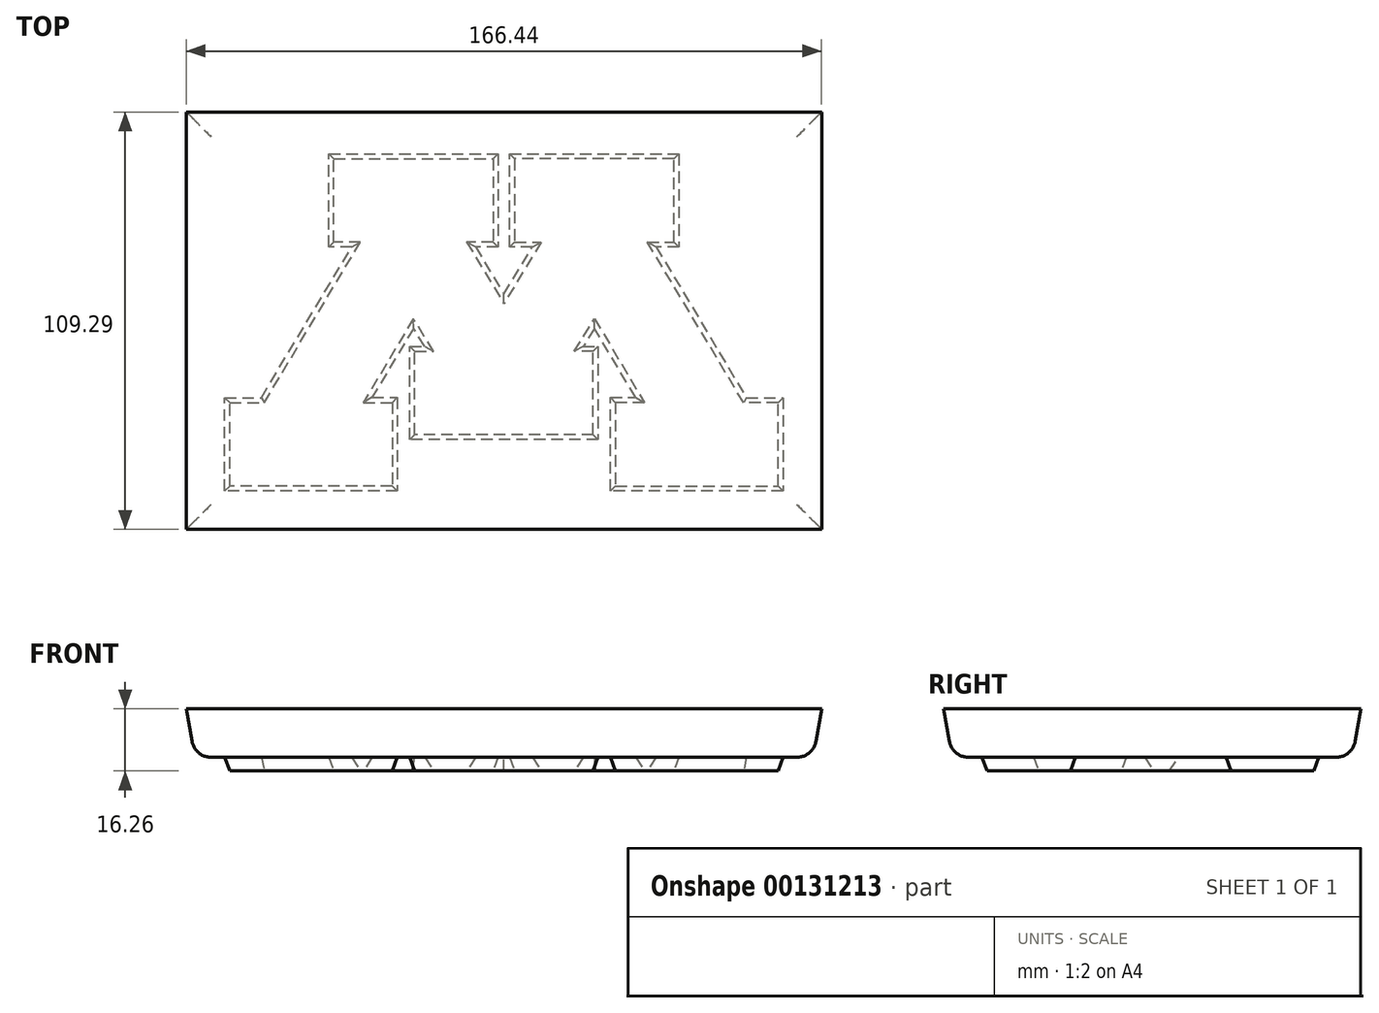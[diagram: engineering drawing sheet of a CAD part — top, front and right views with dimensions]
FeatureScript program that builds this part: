
annotation { "Feature Type Name" : "Feature", "Feature Type Description" : "" }
export const myFeature = defineFeature(function(context is Context, id is Id, definition is map)
    precondition{}
    {
        {
            var Q0;
            Q0=qCreatedBy(makeId("Top.planeOp"),FACE);
            var sketch = newSketch(context, id + "F0", { "sketchPlane" : qUnion([Q0])});
            skLineSegment(sketch, "E0", {"start": v(0, 13.9) * mm, "end": v(-9.74, 30.03) * mm});
            skLineSegment(sketch, "E1", {"start": v(-9.74, 30.03) * mm, "end": v(-2.82, 30.03) * mm});
            skLineSegment(sketch, "E2", {"start": v(-2.82, 30.03) * mm, "end": v(-2.82, 51.81) * mm});
            skLineSegment(sketch, "E3", {"start": v(-2.82, 51.81) * mm, "end": v(-44.55, 51.81) * mm});
            skLineSegment(sketch, "E4", {"start": v(-44.55, 51.81) * mm, "end": v(-44.55, 30.06) * mm});
            skLineSegment(sketch, "E5", {"start": v(-44.55, 30.06) * mm, "end": v(-37.59, 30.06) * mm});
            skLineSegment(sketch, "E6", {"start": v(-37.59, 30.06) * mm, "end": v(-62.78, -12) * mm});
            skLineSegment(sketch, "E7", {"start": v(-62.78, -12) * mm, "end": v(-71.82, -12) * mm});
            skLineSegment(sketch, "E8", {"start": v(-71.82, -12) * mm, "end": v(-71.82, -33.84) * mm});
            skLineSegment(sketch, "E9", {"start": v(-71.82, -33.84) * mm, "end": v(-29.23, -33.84) * mm});
            skLineSegment(sketch, "E10", {"start": v(-29.23, -33.84) * mm, "end": v(-29.23, -11.96) * mm});
            skLineSegment(sketch, "E11", {"start": v(-29.23, -11.96) * mm, "end": v(-36.81, -11.96) * mm});
            skLineSegment(sketch, "E12", {"start": v(-36.81, -11.96) * mm, "end": v(-23.72, 9.93) * mm});
            skLineSegment(sketch, "E13", {"start": v(-23.72, 9.93) * mm, "end": v(-18.44, 1.4) * mm});
            skLineSegment(sketch, "E14", {"start": v(-18.44, 1.4) * mm, "end": v(-23.37, 1.4) * mm});
            skLineSegment(sketch, "E15", {"start": v(-23.37, 1.4) * mm, "end": v(-23.37, -20.36) * mm});
            skLineSegment(sketch, "E16", {"start": v(-23.37, -20.36) * mm, "end": v(0, -20.36) * mm});
            skLineSegment(sketch, "E17", {"start": v(0, -20.36) * mm, "end": v(0, 13.9) * mm});
            skSolve(sketch);
        }
        {
            var Q0;
            Q0=qSketchRegion(id+"F0",true);
            extrude(context, id + "F1", {"entities" : qUnion([Q0]), "depth" : 12.45 * mm, "hasDraft" : true, "draftAngle" : 20 * degree});
        }
        {
            var Q0;
            Q0=makeQuery(id+"F1.opExtrude","SWEPT_BODY",BODY,{"disambiguationData":[OSD([sQuery(id+"F0.wireOp",EDGE,"E0"),sQuery(id+"F0.wireOp",EDGE,"E1"),sQuery(id+"F0.wireOp",EDGE,"E2"),sQuery(id+"F0.wireOp",EDGE,"E3"),sQuery(id+"F0.wireOp",EDGE,"E4"),sQuery(id+"F0.wireOp",EDGE,"E5"),sQuery(id+"F0.wireOp",EDGE,"E6"),sQuery(id+"F0.wireOp",EDGE,"E7"),sQuery(id+"F0.wireOp",EDGE,"E8"),sQuery(id+"F0.wireOp",EDGE,"E9"),sQuery(id+"F0.wireOp",EDGE,"E10"),sQuery(id+"F0.wireOp",EDGE,"E11"),sQuery(id+"F0.wireOp",EDGE,"E12"),sQuery(id+"F0.wireOp",EDGE,"E13"),sQuery(id+"F0.wireOp",EDGE,"E14"),sQuery(id+"F0.wireOp",EDGE,"E15"),sQuery(id+"F0.wireOp",EDGE,"E16"),sQuery(id+"F0.wireOp",EDGE,"E17")])]});
            var Q1;
            Q1=qCreatedBy(makeId("Right.planeOp"),FACE);
            mirror(context, id + "F2", {"operationType" : NewBodyOperationType.ADD, "entities" : qUnion([Q0]), "mirrorPlane" : qUnion([Q1])});
        }
        {
            var Q0;
            {var subQ0=makeQuery(id+"F1.opExtrude","CAP_FACE",FACE,{"disambiguationData":[OSD([sQuery(id+"F0.wireOp",EDGE,"E0"),sQuery(id+"F0.wireOp",EDGE,"E1"),sQuery(id+"F0.wireOp",EDGE,"E2"),sQuery(id+"F0.wireOp",EDGE,"E3"),sQuery(id+"F0.wireOp",EDGE,"E4"),sQuery(id+"F0.wireOp",EDGE,"E5"),sQuery(id+"F0.wireOp",EDGE,"E6"),sQuery(id+"F0.wireOp",EDGE,"E7"),sQuery(id+"F0.wireOp",EDGE,"E8"),sQuery(id+"F0.wireOp",EDGE,"E9"),sQuery(id+"F0.wireOp",EDGE,"E10"),sQuery(id+"F0.wireOp",EDGE,"E11"),sQuery(id+"F0.wireOp",EDGE,"E12"),sQuery(id+"F0.wireOp",EDGE,"E13"),sQuery(id+"F0.wireOp",EDGE,"E14"),sQuery(id+"F0.wireOp",EDGE,"E15"),sQuery(id+"F0.wireOp",EDGE,"E16"),sQuery(id+"F0.wireOp",EDGE,"E17")])],"isStart":false});Q0=makeQuery(id+"F2.boolean.opBoolean","MERGE",FACE,{"derivedFrom":[subQ0,makeQuery(id+"F2.opPattern","COPY",FACE,{"derivedFrom":subQ0,"instanceName":"1"})]});}
            var sketch = newSketch(context, id + "F3", { "sketchPlane" : qUnion([Q0])});
            skLineSegment(sketch, "E18.bottom", {"start": v(-82.55, -44.51) * mm, "end": v(82.55, -44.51) * mm});
            skLineSegment(sketch, "E18.top", {"start": v(-82.55, 63.44) * mm, "end": v(82.55, 63.44) * mm});
            skLineSegment(sketch, "E18.left", {"start": v(-82.55, -44.51) * mm, "end": v(-82.55, 63.44) * mm});
            skLineSegment(sketch, "E18.right", {"start": v(82.55, -44.51) * mm, "end": v(82.55, 63.44) * mm});
            skPoint(sketch, "E18.middle", {"position": v(0, 9.46) * mm});
            skSolve(sketch);
        }
        {
            var Q0;
            Q0 = qSketchRegion(id + "F3", true);
            extrude(context, id + "F4", {"entities" : qUnion([Q0]), "operationType" : NewBodyOperationType.ADD, "oppositeDirection" : true, "depth" : 8.9 * mm, "hasDraft" : true, "draftAngle" : 10 * degree, "draftPullDirection" : true});
        }
        {
            var Q0;
            {var subQ0=makeQuery(id+"F1.opExtrude","CAP_FACE",FACE,{"disambiguationData":[OSD([sQuery(id+"F0.wireOp",EDGE,"E0"),sQuery(id+"F0.wireOp",EDGE,"E1"),sQuery(id+"F0.wireOp",EDGE,"E2"),sQuery(id+"F0.wireOp",EDGE,"E3"),sQuery(id+"F0.wireOp",EDGE,"E4"),sQuery(id+"F0.wireOp",EDGE,"E5"),sQuery(id+"F0.wireOp",EDGE,"E6"),sQuery(id+"F0.wireOp",EDGE,"E7"),sQuery(id+"F0.wireOp",EDGE,"E8"),sQuery(id+"F0.wireOp",EDGE,"E9"),sQuery(id+"F0.wireOp",EDGE,"E10"),sQuery(id+"F0.wireOp",EDGE,"E11"),sQuery(id+"F0.wireOp",EDGE,"E12"),sQuery(id+"F0.wireOp",EDGE,"E13"),sQuery(id+"F0.wireOp",EDGE,"E14"),sQuery(id+"F0.wireOp",EDGE,"E15"),sQuery(id+"F0.wireOp",EDGE,"E16"),sQuery(id+"F0.wireOp",EDGE,"E17")])],"isStart":false});Q0=makeQuery(id+"F4.boolean.opBoolean","MERGE",FACE,{"derivedFrom":[makeQuery(id+"F2.boolean.opBoolean","MERGE",FACE,{"derivedFrom":[subQ0,makeQuery(id+"F2.opPattern","COPY",FACE,{"derivedFrom":subQ0,"instanceName":"1"})]}),makeQuery(id+"F4.opExtrude","CAP_FACE",FACE,{"disambiguationData":[OSD([sQuery(id+"F3.wireOp",EDGE,"E18.bottom"),sQuery(id+"F3.wireOp",EDGE,"E18.top"),sQuery(id+"F3.wireOp",EDGE,"E18.left"),sQuery(id+"F3.wireOp",EDGE,"E18.right")])],"isStart":true})]});}
            extrude(context, id + "F5", {"entities" : qUnion([Q0]), "operationType" : NewBodyOperationType.ADD, "depth" : 3.8 * mm, "hasDraft" : true, "draftAngle" : 10 * degree});
        }
        {
            var Q0;
            Q0=makeQuery(id+"F4.opExtrude","CAP_EDGE",EDGE,{"disambiguationData":[OSD([sQuery(id+"F3.wireOp",EDGE,"E18.right")])],"isStart":false});
            var Q1;
            Q1=makeQuery(id+"F4.opExtrude","CAP_EDGE",EDGE,{"disambiguationData":[OSD([sQuery(id+"F3.wireOp",EDGE,"E18.top")])],"isStart":false});
            var Q2;
            Q2=makeQuery(id+"F4.opExtrude","CAP_EDGE",EDGE,{"disambiguationData":[OSD([sQuery(id+"F3.wireOp",EDGE,"E18.bottom")])],"isStart":false});
            var Q3;
            Q3=makeQuery(id+"F4.opExtrude","CAP_EDGE",EDGE,{"disambiguationData":[OSD([sQuery(id+"F3.wireOp",EDGE,"E18.left")])],"isStart":false});
            fillet(context, id + "F6", {"entities" : qUnion([Q0, Q1, Q2, Q3]), "radius" : 5.08 * mm, "tangentPropagation" : true, "allowEdgeOverflow" : false});
        }
    });
